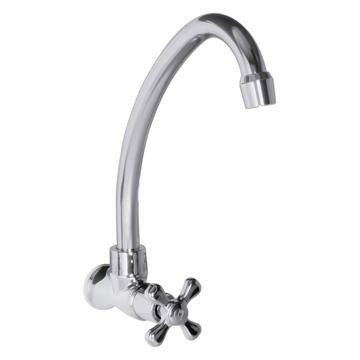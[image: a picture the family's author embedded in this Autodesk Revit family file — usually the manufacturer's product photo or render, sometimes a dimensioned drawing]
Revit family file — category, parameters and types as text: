
# Revit family: 01-1353-11-LLAVE MÓVIL PARED C CUERPO PLÁSTICO ATLÁNTICO
name_source: partatom
category: Plumbing Fixtures
revit_build: Autodesk Revit 2018 (Build: 20170223_1515(x64)
units: mm (PartAtom-declared; Revit-internal decimal feet)

## family parameters
Cut with Voids When Loaded = No
Host = Face
OmniClass Number = 23.31.11.00
Part Type = Normal
Room Calculation Point = No
Round Connector Dimension = Use Diameter
Shared = No

## types (1)
- 01-1353-11
    Alto = 298 mm
    Alto cuerpo-llave = 120 mm  [stored 0.393701 ft]
    Ancho  manija = 66 mm  [stored 0.216535 ft]
    CW Connection = Yes
    Default Elevation = 0 mm  [stored 0 ft]
    Description = Monomando
    HW Connection = Yes
    Link Ficha Tecnica = http://infotecnica.gricol.com
    Manufacturer = Gricol
    Model = 01-1353-11
    Plástico - ABS Cromado = Plastico ABS Cromado
    Product Name = LLAVE MÓVIL PARED C CUERPO PLÁSTICO ATLÁNTICO
    Profundidad = 160 mm  [stored 0.524934 ft]
    Type Image = 01-1353-11-FOTO LLAVE MÓVIL PARED C CUERPO ATLÁNTICO.jpg
    URL = https://www.gricol.com
    Vent Connection = No
    Waste Connection = No

note: [stored X ft] marks values corroborated as IEEE doubles in the binary element streams (Revit-internal decimal feet)

## geometry (parser evidence)
native form markers: Blend x2, Sweep x6
no freeform markers — native parametric forms only
